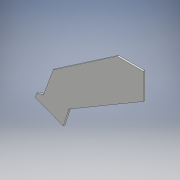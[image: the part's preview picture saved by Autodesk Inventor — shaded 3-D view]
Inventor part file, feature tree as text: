
AUTODESK INVENTOR PART (.ipt)
format: ipt  version: 2018 (Build 220112000, 112)  size: 103,424 bytes
history: native  units: mm
features: extrude x1, sketch x1
ambient origin geometry x8: Origin, YZ Plane, XZ Plane, XY Plane, X Axis, Y Axis, Z Axis, Center Point
bodies: Solide1 (feature_tree)
feature tree (2):
  extrude  "Extrusion1"  Depth=45.0mm
  sketch  "Esquisse1"
